FCSTD DOCUMENT  (FreeCAD 0.20R29177 (Git))
Label: Haut7PoucesOreille
License: All rights reserved
LicenseURL: http://en.wikipedia.org/wiki/All_rights_reserved
objects: Sketcher::SketchObject×1, PartDesign::Body×1
note: 2 computed .brp shape members not serialized (recipe doc carries the construction recipe); baked Part::Feature solids carry a one-line shape summary decoded from their .brp
EXTERNAL_REF file=DonneesBoitier.FCStd obj=Spreadsheet

FEATURE [Sketcher::SketchObject] Sketch
  FullyConstrained = true
  MapMode = 5
  Support = -> [XY_Plane]
  expr: Constraints[113] = <<DonneesBoitier>>#<<Spreadsheet>>.xxLongEncoches
  expr: Constraints[119] = <<DonneesBoitier>>#<<Spreadsheet>>.xxLargEconche
  expr: Constraints[125] = <<DonneesBoitier>>#<<Spreadsheet>>.xxEpEcrou
  expr: Constraints[130] = <<DonneesBoitier>>#<<Spreadsheet>>.xxDiametreTrou
  expr: Constraints[131] = <<DonneesBoitier>>#<<Spreadsheet>>.xxDiametreTrou
  expr: Constraints[134] = <<DonneesBoitier>>#<<Spreadsheet>>.xxDistEcrou
  expr: Constraints[135] = <<DonneesBoitier>>#<<Spreadsheet>>.xxLongVis
  expr: Constraints[139] = <<DonneesBoitier>>#<<Spreadsheet>>.xxDiametreTrou
  expr: Constraints[149] = <<DonneesBoitier>>#Spreadsheet.xxLargLatHaut
  expr: Constraints[151] = DonneesBoitier#<<Spreadsheet>>.xxLongDessus
  expr: Constraints[152] = <<DonneesBoitier>>#<<Spreadsheet>>.xxLargeurEncasEcran / 4 - <<DonneesBoitier>>#<<Spreadsheet>>.xxLargEconche / 2
  expr: Constraints[154] = <<DonneesBoitier>>#<<Spreadsheet>>.xxLargeurEncasEcran / 4 - <<DonneesBoitier>>#<<Spreadsheet>>.xxLargEconche / 2
  sketch-geometry (56):
    g0: LineSegment StartX=-67.5 StartY=32.5 StartZ=0 EndX=-32.5 EndY=32.5 EndZ=0
    g1: LineSegment StartX=-32.5 StartY=32.5 StartZ=0 EndX=-32.5 EndY=37.5 EndZ=0
    g2: LineSegment StartX=-32.5 StartY=37.5 StartZ=0 EndX=-17.5 EndY=37.5 EndZ=0
    g3: LineSegment StartX=-17.5 StartY=37.5 StartZ=0 EndX=-17.5 EndY=32.5 EndZ=0
    g4: LineSegment StartX=-17.5 StartY=32.5 StartZ=0 EndX=-2.625 EndY=32.5 EndZ=0
    g5: LineSegment StartX=-2.625 StartY=32.5 StartZ=0 EndX=-2.625 EndY=27.5 EndZ=0
    g6: LineSegment StartX=-2.625 StartY=27.5 StartZ=0 EndX=-4 EndY=27.5 EndZ=0
    g7: LineSegment StartX=-4 StartY=27.5 StartZ=0 EndX=-4 EndY=23.5 EndZ=0
    g8: LineSegment StartX=-4 StartY=23.5 StartZ=0 EndX=-2.625 EndY=23.5 EndZ=0
    g9: LineSegment StartX=-2.625 StartY=23.5 StartZ=0 EndX=-2.625 EndY=20.5 EndZ=0
    g10: LineSegment StartX=-2.625 StartY=20.5 StartZ=0 EndX=2.625 EndY=20.5 EndZ=0
    g11: LineSegment StartX=2.625 StartY=20.5 StartZ=0 EndX=2.625 EndY=23.5 EndZ=0
    g12: LineSegment StartX=2.625 StartY=23.5 StartZ=0 EndX=4 EndY=23.5 EndZ=0
    g13: LineSegment StartX=4 StartY=23.5 StartZ=0 EndX=4 EndY=27.5 EndZ=0
    g14: LineSegment StartX=4 StartY=27.5 StartZ=0 EndX=2.625 EndY=27.5 EndZ=0
    g15: LineSegment StartX=2.625 StartY=27.5 StartZ=0 EndX=2.625 EndY=32.5 EndZ=0
    g16: LineSegment StartX=2.625 StartY=32.5 StartZ=0 EndX=17.5 EndY=32.5 EndZ=0
    g17: LineSegment StartX=17.5 StartY=32.5 StartZ=0 EndX=17.5 EndY=37.5 EndZ=0
    g18: LineSegment StartX=17.5 StartY=37.5 StartZ=0 EndX=32.5 EndY=37.5 EndZ=0
    g19: LineSegment StartX=32.5 StartY=37.5 StartZ=0 EndX=32.5 EndY=32.5 EndZ=0
    g20: LineSegment StartX=32.5 StartY=32.5 StartZ=0 EndX=67.5 EndY=32.5 EndZ=0
    g21: LineSegment StartX=67.5 StartY=32.5 StartZ=0 EndX=67.5 EndY=7.5 EndZ=0
    g22: LineSegment StartX=67.5 StartY=7.5 StartZ=0 EndX=72.5 EndY=7.5 EndZ=0
    g23: LineSegment StartX=72.5 StartY=7.5 StartZ=0 EndX=72.5 EndY=-7.5 EndZ=0
    g24: LineSegment StartX=72.5 StartY=-7.5 StartZ=0 EndX=67.5 EndY=-7.5 EndZ=0
    g25: LineSegment StartX=67.5 StartY=-7.5 StartZ=0 EndX=67.5 EndY=-32.5 EndZ=0
    g26: LineSegment StartX=67.5 StartY=-32.5 StartZ=0 EndX=32.5 EndY=-32.5 EndZ=0
    g27: LineSegment StartX=32.5 StartY=-32.5 StartZ=0 EndX=32.5 EndY=-37.5 EndZ=0
    g28: LineSegment StartX=32.5 StartY=-37.5 StartZ=0 EndX=17.5 EndY=-37.5 EndZ=0
    g29: LineSegment StartX=17.5 StartY=-37.5 StartZ=0 EndX=17.5 EndY=-32.5 EndZ=0
    g30: LineSegment StartX=17.5 StartY=-32.5 StartZ=0 EndX=2.625 EndY=-32.5 EndZ=0
    g31: LineSegment StartX=2.625 StartY=-32.5 StartZ=0 EndX=2.625 EndY=-27.5 EndZ=0
    g32: LineSegment StartX=2.625 StartY=-27.5 StartZ=0 EndX=4 EndY=-27.5 EndZ=0
    g33: LineSegment StartX=4 StartY=-27.5 StartZ=0 EndX=4 EndY=-23.5 EndZ=0
    g34: LineSegment StartX=4 StartY=-23.5 StartZ=0 EndX=2.625 EndY=-23.5 EndZ=0
    g35: LineSegment StartX=2.625 StartY=-23.5 StartZ=0 EndX=2.625 EndY=-20.5 EndZ=0
    g36: LineSegment StartX=2.625 StartY=-20.5 StartZ=0 EndX=-2.625 EndY=-20.5 EndZ=0
    g37: LineSegment StartX=-2.625 StartY=-20.5 StartZ=0 EndX=-2.625 EndY=-23.5 EndZ=0
    g38: LineSegment StartX=-2.625 StartY=-23.5 StartZ=0 EndX=-4 EndY=-23.5 EndZ=0
    g39: LineSegment StartX=-4 StartY=-23.5 StartZ=0 EndX=-4 EndY=-27.5 EndZ=0
    g40: LineSegment StartX=-4 StartY=-27.5 StartZ=0 EndX=-2.625 EndY=-27.5 EndZ=0
    g41: LineSegment StartX=-2.625 StartY=-27.5 StartZ=0 EndX=-2.625 EndY=-32.5 EndZ=0
    g42: LineSegment StartX=-2.625 StartY=-32.5 StartZ=0 EndX=-17.5 EndY=-32.5 EndZ=0
    g43: LineSegment StartX=-17.5 StartY=-32.5 StartZ=0 EndX=-17.5 EndY=-37.5 EndZ=0
    g44: LineSegment StartX=-17.5 StartY=-37.5 StartZ=0 EndX=-32.5 EndY=-37.5 EndZ=0
    g45: LineSegment StartX=-32.5 StartY=-37.5 StartZ=0 EndX=-32.5 EndY=-32.5 EndZ=0
    g46: LineSegment StartX=-32.5 StartY=-32.5 StartZ=0 EndX=-67.5 EndY=-32.5 EndZ=0
    g47: LineSegment StartX=-67.5 StartY=-32.5 StartZ=0 EndX=-67.5 EndY=-7.5 EndZ=0
    g48: LineSegment StartX=-67.5 StartY=-7.5 StartZ=0 EndX=-72.5 EndY=-7.5 EndZ=0
    g49: LineSegment StartX=-72.5 StartY=-7.5 StartZ=0 EndX=-72.5 EndY=7.5 EndZ=0
    g50: LineSegment StartX=-72.5 StartY=7.5 StartZ=0 EndX=-67.5 EndY=7.5 EndZ=0
    g51: LineSegment StartX=-67.5 StartY=7.5 StartZ=0 EndX=-67.5 EndY=32.5 EndZ=0
    g52: LineSegment StartX=-155.05 StartY=32.5 StartZ=0 EndX=157.34 EndY=32.5 EndZ=0
    g53: LineSegment StartX=67.5 StartY=56.72 StartZ=0 EndX=67.5 EndY=-45.82 EndZ=0
    g54: LineSegment StartX=-155.05 StartY=-32.5 StartZ=0 EndX=157.34 EndY=-32.5 EndZ=0
    g55: LineSegment StartX=-67.5 StartY=56.72 StartZ=0 EndX=-67.5 EndY=-45.82 EndZ=0
  constraints (161):
    c: Horizontal(g0)
    c: Coincident(g0,g1)
    c: Vertical(g1)
    c: Coincident(g1,g2)
    c: Horizontal(g2)
    c: Coincident(g2,g3)
    c: Coincident(g3,g4)
    c: Horizontal(g4)
    c: Coincident(g4,g5)
    c: Horizontal(g6)
    c: Coincident(g6,g7)
    c: Coincident(g7,g8)
    c: Horizontal(g8)
    c: Coincident(g8,g9)
    c: Vertical(g9)
    c: Coincident(g9,g10)
    c: Coincident(g10,g11)
    c: Coincident(g11,g12)
    c: Coincident(g12,g13)
    c: Vertical(g13)
    c: Coincident(g13,g14)
    c: Coincident(g14,g15)
    c: Coincident(g15,g16)
    c: Horizontal(g16)
    c: Coincident(g16,g17)
    c: Coincident(g17,g18)
    c: Horizontal(g18)
    c: Coincident(g18,g19)
    c: Vertical(g19)
    c: Coincident(g19,g20)
    c: Horizontal(g20)
    c: Coincident(g20,g21)
    c: Vertical(g21)
    c: Coincident(g21,g22)
    c: Horizontal(g22)
    c: Coincident(g22,g23)
    c: Vertical(g23)
    c: Coincident(g23,g24)
    c: Coincident(g24,g25)
    c: Coincident(g25,g26)
    c: Horizontal(g26)
    c: Coincident(g26,g27)
    c: Vertical(g27)
    c: Coincident(g27,g28)
    c: Horizontal(g28)
    c: Coincident(g28,g29)
    c: Vertical(g29)
    c: Coincident(g29,g30)
    c: Horizontal(g30)
    c: Coincident(g30,g31)
    c: Coincident(g31,g32)
    c: Coincident(g32,g33)
    c: Coincident(g33,g34)
    c: Horizontal(g34)
    c: Coincident(g34,g35)
    c: Vertical(g35)
    c: Coincident(g35,g36)
    c: Coincident(g36,g37)
    c: Vertical(g37)
    c: Coincident(g37,g38)
    c: Horizontal(g38)
    c: Coincident(g38,g39)
    c: Coincident(g39,g40)
    c: Horizontal(g40)
    c: Coincident(g40,g41)
    c: Vertical(g41)
    c: Coincident(g41,g42)
    c: Coincident(g42,g43)
    c: Vertical(g43)
    c: Coincident(g43,g44)
    c: Horizontal(g44)
    c: Coincident(g44,g45)
    c: Vertical(g45)
    c: Coincident(g45,g46)
    c: Horizontal(g46)
    c: Coincident(g46,g47)
    c: Vertical(g47)
    c: Coincident(g47,g48)
    c: Horizontal(g48)
    c: Coincident(g48,g49)
    c: Vertical(g49)
    c: Coincident(g49,g50)
    c: Horizontal(g50)
    c: Coincident(g50,g51)
    c: Coincident(g51,g0)
    c: Vertical(g51)
    c: Vertical(g31)
    c: Vertical(g33)
    c: Vertical(g39)
    c: Vertical(g7)
    c: Vertical(g11)
    c: Vertical(g17)
    c: Vertical(g3)
    c: Vertical(g15)
    c: Vertical(g5)
    c: Coincident(g6,g5)
    c: Horizontal(g10)
    c: Horizontal(g12)
    c: Horizontal(g24)
    c: Horizontal(g32)
    c: Horizontal(g52)
    c: Vertical(g53)
    c: Horizontal(g54)
    c: Vertical(g55)
    c: PointOnObject(g0,g52)
    c: PointOnObject(g0,g55)
    c: PointOnObject(g46,g54)
    c: PointOnObject(g42,g54)
    c: PointOnObject(g25,g53)
    c: PointOnObject(g20,g52)
    c: PointOnObject(g16,g52)
    c: Distance(g52) = 312.39
    c: Equal(g52,g54)
    c: DistanceY(g1,g1) = 5
    c: Equal(g1,g50)
    c: Equal(g50,g45)
    c: Equal(g45,g29)
    c: Equal(g29,g24)
    c: Equal(g24,g19)
    c: DistanceX(g2,g2) = 15
    c: Equal(g2,g18)
    c: Equal(g18,g23)
    c: Equal(g23,g28)
    c: Equal(g28,g44)
    c: Equal(g44,g49)
    c: DistanceY(g7,g7) = 4
    c: Equal(g13,g33)
    c: Equal(g33,g39)
    c: Symmetric(g5,g14,g-2)
    c: Symmetric(g8,g11,g-2)
    c: DistanceX(g10,g10) = 5.25
    c: DistanceX(g4,g15) = 5.25
    c: DistanceX(g6,g13) = 8
    c: Symmetric(g6,g13,g-2)
    c: DistanceY(g5,g4) = 5
    c: DistanceY(g10,g15) = 12
    c: Symmetric(g3,g16,g-2)
    c: Symmetric(g29,g42,g-2)
    c: Equal(g10,g36)
    c: DistanceX(g41,g30) = 5.25
    c: Symmetric(g30,g41,g-2)
    c: Symmetric(g36,g35,g-2)
    c: Equal(g15,g31)
    c: Equal(g31,g41)
    c: Equal(g11,g35)
    c: Equal(g34,g38)
    c: Equal(g38,g14)
    c: Symmetric(g47,g50,g-1)
    c: Symmetric(g24,g21,g-1)
    c: DistanceY(g25,g20) = 65
    c: Symmetric(g20,g25,g-1)
    c: DistanceX(g0,g20) = 135
    c: DistanceX(g3,g-1) = 17.5
    c: Symmetric(g46,g25,g-2)
    c: DistanceX(g42,g-1) = 17.5
    c: DistanceY(g53,g55) = 0
    c: DistanceX(g54,g52) = 0
    c: DistanceY(g55,g53) = 0
    c: DistanceX(g52,g-1) = 155.05
    c: DistanceY(g53,g-1) = 45.82
    c: DistanceY(g-1,g53) = 56.72
FEATURE [PartDesign::Body] Body  label="Body-Haut"
  Group = -> [Sketch]
  Origin = -> Origin
